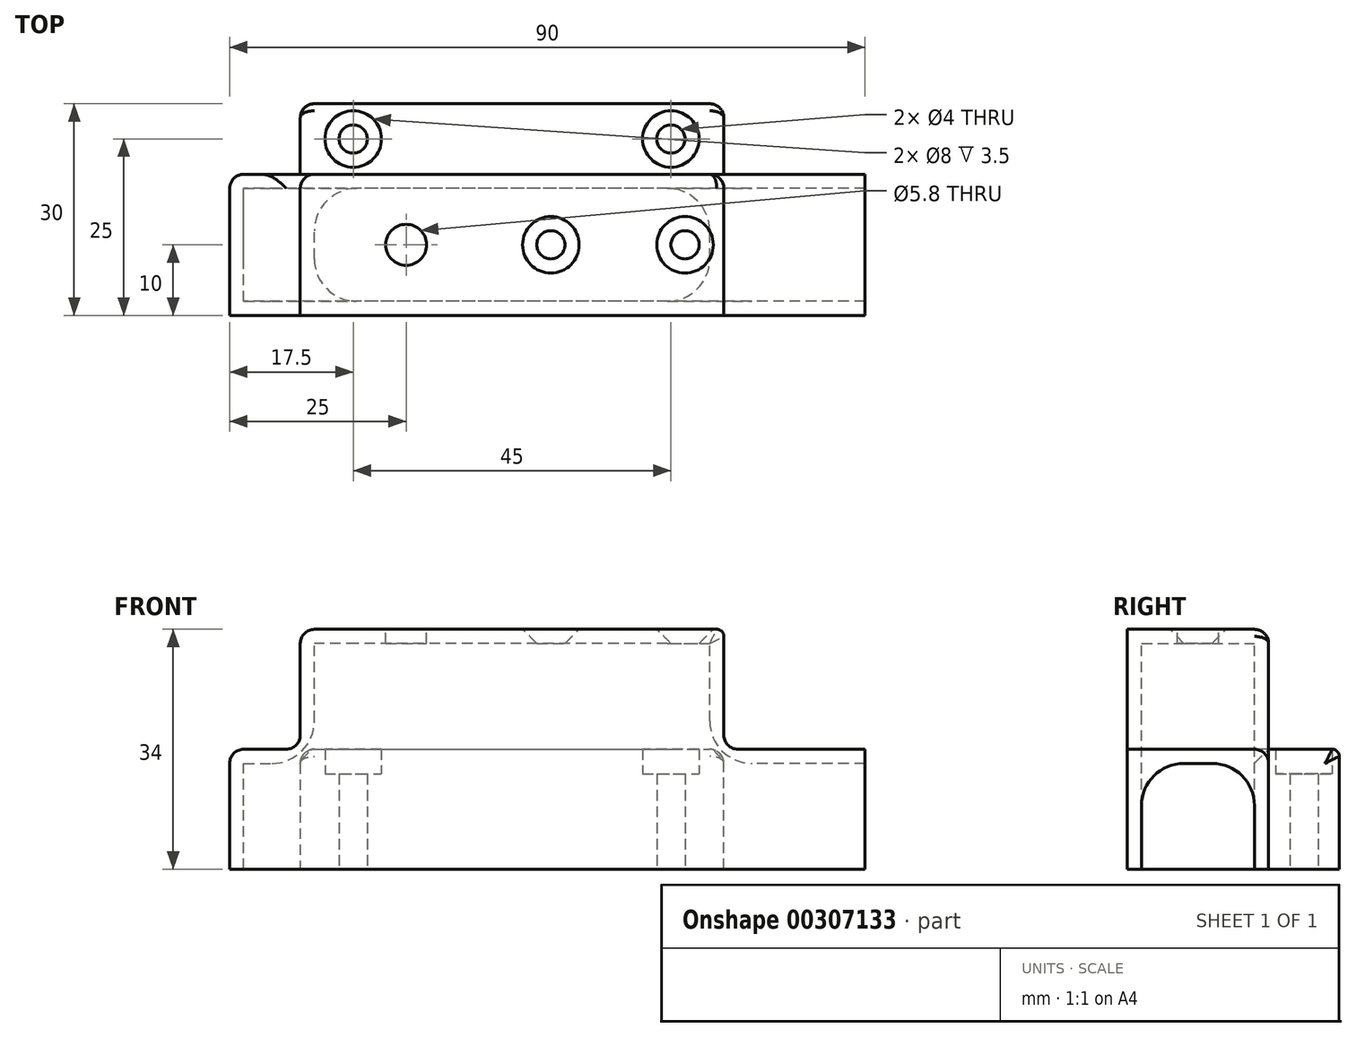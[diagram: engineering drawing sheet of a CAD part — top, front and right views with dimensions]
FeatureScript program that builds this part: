
annotation { "Feature Type Name" : "Feature", "Feature Type Description" : "" }
export const myFeature = defineFeature(function(context is Context, id is Id, definition is map)
    precondition{}
    {
        {
            var Q0;
            Q0=qCreatedBy(makeId("Front.planeOp"),FACE);
            var sketch = newSketch(context, id + "F0", { "sketchPlane" : qUnion([Q0])});
            skLineSegment(sketch, "E0", {"start": v(0, 0) * mm, "end": v(-40, 0) * mm});
            skLineSegment(sketch, "E1", {"start": v(-40, 0) * mm, "end": v(-40, 17) * mm});
            skLineSegment(sketch, "E2", {"start": v(-40, 17) * mm, "end": v(-30, 17) * mm});
            skLineSegment(sketch, "E3", {"start": v(-30, 17) * mm, "end": v(-30, 34) * mm});
            skLineSegment(sketch, "E4", {"start": v(-30, 34) * mm, "end": v(0, 34) * mm});
            skLineSegment(sketch, "E5.MirrorCS", {"start": v(30, 34) * mm, "end": v(0, 34) * mm});
            skLineSegment(sketch, "E6.MirrorCS", {"start": v(30, 17) * mm, "end": v(30, 34) * mm});
            skLineSegment(sketch, "E7.MirrorCS", {"start": v(50, 17) * mm, "end": v(30, 17) * mm});
            skLineSegment(sketch, "E8.MirrorCS", {"start": v(50, 0) * mm, "end": v(50, 17) * mm});
            skLineSegment(sketch, "E9.MirrorCS", {"start": v(0, 0) * mm, "end": v(50, 0) * mm});
            skLineSegment(sketch, "E10", {"start": v(-30, 17) * mm, "end": v(30, 17) * mm});
            skLineSegment(sketch, "E11", {"start": v(30, 0) * mm, "end": v(30, 17) * mm});
            skLineSegment(sketch, "E12", {"start": v(-30, 17) * mm, "end": v(-30, 0) * mm});
            skSolve(sketch);
        }
        {
            var Q0;
            Q0 = qSketchRegion(id + "F0", true);
            var Q1;
            Q1=makeQuery(id+"F0.imprint","IMPRINT",FACE,{"disambiguationData":[TD([[makeQuery(id+"F0.imprint","IMPRINT",EDGE,{"derivedFrom":sQuery(id+"F0.wireOp",EDGE,"E0")}),-1.0]])]});
            extrude(context, id + "F1", {"entities" : qUnion([Q0, Q1]), "depth" : 20 * mm});
        }
        {
            var Q0;
            Q0=makeQuery(id+"F1.opExtrude","SWEPT_FACE",FACE,{"disambiguationData":[OSD([sQuery(id+"F0.wireOp",EDGE,"E0"),sQuery(id+"F0.wireOp",EDGE,"E9.MirrorCS")])]});
            shell(context, id + "F2", {"entities" : qUnion([Q0]), "thickness" : 2 * mm});
        }
        {
            var Q0;
            Q0=makeQuery(id+"F1.opExtrude","SWEPT_FACE",FACE,{"disambiguationData":[OSD([sQuery(id+"F0.wireOp",EDGE,"E4"),sQuery(id+"F0.wireOp",EDGE,"E5.MirrorCS")])]});
            var sketch = newSketch(context, id + "F3", { "sketchPlane" : qUnion([Q0])});
            skLineSegment(sketch, "E13", {"start": v(0, 0) * mm, "end": v(0, -20) * mm});
            skLineSegment(sketch, "E14", {"start": v(0, -10) * mm, "end": v(-30, -10) * mm});
            skCircle(sketch, "E15", {"center": v(-15, -10) * mm, "radius": 2.9 * mm});
            skLineSegment(sketch, "E16.MirrorCS", {"start": v(0, -10) * mm, "end": v(30, -10) * mm});
            skLineSegment(sketch, "E17", {"start": v(15, -10) * mm, "end": v(11, -10) * mm});
            skLineSegment(sketch, "E18", {"start": v(11, -10) * mm, "end": v(11, -6.5) * mm});
            skLineSegment(sketch, "E19", {"start": v(11, -6.5) * mm, "end": v(15, -6.5) * mm});
            skLineSegment(sketch, "E20", {"start": v(15, -10) * mm, "end": v(15, -8.98) * mm});
            skLineSegment(sketch, "E21.MirrorCS", {"start": v(19, -10) * mm, "end": v(19, -6.5) * mm});
            skLineSegment(sketch, "E22.MirrorCS", {"start": v(19, -6.5) * mm, "end": v(15, -6.5) * mm});
            skLineSegment(sketch, "E23.MirrorCS", {"start": v(11, -10) * mm, "end": v(11, -13.5) * mm});
            skLineSegment(sketch, "E24.MirrorCS", {"start": v(11, -13.5) * mm, "end": v(15, -13.5) * mm});
            skLineSegment(sketch, "E25.MirrorCS", {"start": v(19, -13.5) * mm, "end": v(15, -13.5) * mm});
            skLineSegment(sketch, "E26.MirrorCS", {"start": v(19, -10) * mm, "end": v(19, -13.5) * mm});
            skLineSegment(sketch, "E27", {"start": v(19, -10) * mm, "end": v(30, -10) * mm});
            skLineSegment(sketch, "E28", {"start": v(24.5, -10) * mm, "end": v(24.5, -8.9) * mm});
            skLineSegment(sketch, "E29", {"start": v(11, -10) * mm, "end": v(0, -10) * mm});
            skLineSegment(sketch, "E30", {"start": v(5.5, -10) * mm, "end": v(5.5, -8.97) * mm});
            skSolve(sketch);
        }
        {
            var Q0;
            {var subQ0=sQuery(id+"F3.wireOp",EDGE,"E15");var subQ1=sQuery(id+"F3.wireOp",EDGE,"E14");var subQ2=makeQuery(id+"F3.imprint","INTERSECT",VERTEX,{"disambiguationData":[OD(0.0)],"derivedFrom":[subQ1,subQ0]});Q0=makeQuery(id+"F3.imprint","IMPRINT",FACE,{"disambiguationData":[TD([[makeQuery(id+"F3.imprint","IMPRINT",EDGE,{"disambiguationData":[TD([[subQ2,-1.0]])],"derivedFrom":subQ1}),1.0]])]});}
            var Q1;
            {var subQ0=sQuery(id+"F3.wireOp",EDGE,"E17");Q1=makeQuery(id+"F3.imprint","IMPRINT",FACE,{"disambiguationData":[TD([[makeQuery(id+"F3.imprint","IMPRINT",EDGE,{"derivedFrom":subQ0}),-1.0]])]});}
            var Q2;
            {var subQ0=sQuery(id+"F3.wireOp",EDGE,"E17");Q2=makeQuery(id+"F3.imprint","IMPRINT",FACE,{"disambiguationData":[TD([[makeQuery(id+"F3.imprint","IMPRINT",EDGE,{"derivedFrom":subQ0}),1.0]])]});}
            var Q3;
            {var subQ0=sQuery(id+"F3.wireOp",EDGE,"E15");var subQ1=sQuery(id+"F3.wireOp",EDGE,"E14");var subQ2=makeQuery(id+"F3.imprint","INTERSECT",VERTEX,{"disambiguationData":[OD(0.0)],"derivedFrom":[subQ1,subQ0]});Q3=makeQuery(id+"F3.imprint","IMPRINT",FACE,{"disambiguationData":[TD([[makeQuery(id+"F3.imprint","IMPRINT",EDGE,{"disambiguationData":[TD([[subQ2,-1.0]])],"derivedFrom":subQ1}),-1.0]])]});}
            extrude(context, id + "F4", {"entities" : qUnion([Q0, Q1, Q2, Q3]), "operationType" : NewBodyOperationType.REMOVE, "oppositeDirection" : true, "depth" : 3 * mm});
        }
        {
            var Q0;
            Q0=makeQuery(id+"F2.opShell","OFFSET_FACE",FACE,{"disambiguationData":[OSD([sQuery(id+"F0.wireOp",EDGE,"E8.MirrorCS")])]});
            extrude(context, id + "F5", {"entities" : qUnion([Q0]), "operationType" : NewBodyOperationType.REMOVE, "oppositeDirection" : true, "depth" : 25 * mm});
        }
        {
            var Q0;
            Q0=makeQuery(id+"F2.opShell","OFFSET_EDGE",EDGE,{"disambiguationData":[OSD([sQuery(id+"F0.wireOp",EDGE,"E6.MirrorCS"),sQuery(id+"F0.wireOp",EDGE,"E7.MirrorCS")])]});
            var Q1;
            Q1=makeQuery(id+"F2.opShell","OFFSET_EDGE",EDGE,{"disambiguationData":[OSD([sQuery(id+"F0.wireOp",EDGE,"E2"),sQuery(id+"F0.wireOp",EDGE,"E3")])]});
            fillet(context, id + "F6", {"entities" : qUnion([Q0, Q1]), "radius" : 6 * mm, "tangentPropagation" : true, "allowEdgeOverflow" : false});
        }
        {
            var Q0;
            Q0=makeQuery(id+"F1.opExtrude","SWEPT_EDGE",EDGE,{"disambiguationData":[OSD([sQuery(id+"F0.wireOp",EDGE,"E3"),sQuery(id+"F0.wireOp",EDGE,"E4")])]});
            var Q1;
            Q1=makeQuery(id+"F1.opExtrude","SWEPT_EDGE",EDGE,{"disambiguationData":[OSD([sQuery(id+"F0.wireOp",EDGE,"E1"),sQuery(id+"F0.wireOp",EDGE,"E2")])]});
            var Q2;
            Q2=makeQuery(id+"F1.opExtrude","SWEPT_EDGE",EDGE,{"disambiguationData":[OSD([sQuery(id+"F0.wireOp",EDGE,"E2"),sQuery(id+"F0.wireOp",EDGE,"E3")])]});
            var Q3;
            Q3=makeQuery(id+"F1.opExtrude","CAP_EDGE",EDGE,{"disambiguationData":[OSD([sQuery(id+"F0.wireOp",EDGE,"E4"),sQuery(id+"F0.wireOp",EDGE,"E5.MirrorCS")])],"isStart":true});
            var Q4;
            Q4=makeQuery(id+"F1.opExtrude","CAP_EDGE",EDGE,{"disambiguationData":[OSD([sQuery(id+"F0.wireOp",EDGE,"E6.MirrorCS")])],"isStart":true});
            var Q5;
            Q5=makeQuery(id+"F1.opExtrude","CAP_EDGE",EDGE,{"disambiguationData":[OSD([sQuery(id+"F0.wireOp",EDGE,"E7.MirrorCS")])],"isStart":true});
            var Q6;
            Q6=makeQuery(id+"F1.opExtrude","SWEPT_EDGE",EDGE,{"disambiguationData":[OSD([sQuery(id+"F0.wireOp",EDGE,"E6.MirrorCS"),sQuery(id+"F0.wireOp",EDGE,"E7.MirrorCS")])]});
            var Q7;
            Q7=makeQuery(id+"F1.opExtrude","CAP_EDGE",EDGE,{"disambiguationData":[OSD([sQuery(id+"F0.wireOp",EDGE,"E3")])],"isStart":true});
            var Q8;
            Q8=makeQuery(id+"F1.opExtrude","CAP_EDGE",EDGE,{"disambiguationData":[OSD([sQuery(id+"F0.wireOp",EDGE,"E1")])],"isStart":true});
            fillet(context, id + "F7", {"entities" : qUnion([Q0, Q1, Q2, Q3, Q4, Q5, Q6, Q7, Q8]), "radius" : 2 * mm, "tangentPropagation" : true, "allowEdgeOverflow" : false});
        }
        {
            var Q0;
            Q0=sQuery(id+"F3.wireOp",VERTEX,"E30.start");
            var Q1;
            Q1=sQuery(id+"F3.wireOp",VERTEX,"E28.start");
            var Q2;
            Q2=makeQuery(id+"F1.opExtrude","SWEPT_BODY",BODY,{"disambiguationData":[OSD([sQuery(id+"F0.wireOp",EDGE,"E0"),sQuery(id+"F0.wireOp",EDGE,"E1"),sQuery(id+"F0.wireOp",EDGE,"E2"),sQuery(id+"F0.wireOp",EDGE,"E3"),sQuery(id+"F0.wireOp",EDGE,"E4"),sQuery(id+"F0.wireOp",EDGE,"E5.MirrorCS"),sQuery(id+"F0.wireOp",EDGE,"E6.MirrorCS"),sQuery(id+"F0.wireOp",EDGE,"E7.MirrorCS"),sQuery(id+"F0.wireOp",EDGE,"E8.MirrorCS"),sQuery(id+"F0.wireOp",EDGE,"E9.MirrorCS")])]});
            hole(context, id + "F8", {"style" : HoleStyle.C_SINK, "endStyle" : HoleEndStyle.THROUGH, "holeDiameter" : 2.6 * mm, "cSinkDiameter" : 8 * mm, "cSinkAngle" : 90 * degree, "tappedDepth" : 12 * mm, "tapClearance" : 3, "locations" : qUnion([Q0, Q1]), "scope" : qUnion([Q2]), "startStyle" : HoleStartStyle.PART});
        }
        {
            var Q0;
            Q0=makeQuery(id+"F1.opExtrude","SWEPT_EDGE",EDGE,{"disambiguationData":[OSD([sQuery(id+"F0.wireOp",EDGE,"E5.MirrorCS"),sQuery(id+"F0.wireOp",EDGE,"E6.MirrorCS")])]});
            fillet(context, id + "F9", {"entities" : qUnion([Q0]), "radius" : 1 * mm, "tangentPropagation" : true, "allowEdgeOverflow" : false});
        }
        {
            var Q0;
            Q0=makeQuery(id+"F0.imprint","IMPRINT",FACE,{"disambiguationData":[TD([[makeQuery(id+"F0.imprint","IMPRINT",EDGE,{"derivedFrom":sQuery(id+"F0.wireOp",EDGE,"E10")}),-1.0]])]});
            extrude(context, id + "F10", {"entities" : qUnion([Q0]), "operationType" : NewBodyOperationType.ADD, "oppositeDirection" : true, "depth" : 10 * mm});
        }
        {
            var Q0;
            Q0=makeQuery(id+"F10.opExtrude","SWEPT_FACE",FACE,{"disambiguationData":[OSD([sQuery(id+"F0.wireOp",EDGE,"E10")])]});
            var sketch = newSketch(context, id + "F11", { "sketchPlane" : qUnion([Q0])});
            skLineSegment(sketch, "E31", {"start": v(-30, 5) * mm, "end": v(30, 5) * mm});
            skLineSegment(sketch, "E32", {"start": v(30, 5) * mm, "end": v(0, 5) * mm});
            skLineSegment(sketch, "E33", {"start": v(0, 5) * mm, "end": v(-30, 5) * mm});
            skLineSegment(sketch, "E34", {"start": v(-15, 5) * mm, "end": v(-30, 5) * mm});
            skLineSegment(sketch, "E35", {"start": v(-22.5, 5) * mm, "end": v(-22.5, 8) * mm});
            skLineSegment(sketch, "E36", {"start": v(30, 5) * mm, "end": v(22.5, 5) * mm});
            skSolve(sketch);
        }
        {
            var Q0;
            Q0=sQuery(id+"F11.wireOp",VERTEX,"E35.start");
            var Q1;
            Q1=sQuery(id+"F11.wireOp",VERTEX,"E36.end");
            var Q2;
            Q2=makeQuery(id+"F1.opExtrude","SWEPT_BODY",BODY,{"disambiguationData":[OSD([sQuery(id+"F0.wireOp",EDGE,"E0"),sQuery(id+"F0.wireOp",EDGE,"E1"),sQuery(id+"F0.wireOp",EDGE,"E2"),sQuery(id+"F0.wireOp",EDGE,"E3"),sQuery(id+"F0.wireOp",EDGE,"E4"),sQuery(id+"F0.wireOp",EDGE,"E5.MirrorCS"),sQuery(id+"F0.wireOp",EDGE,"E6.MirrorCS"),sQuery(id+"F0.wireOp",EDGE,"E7.MirrorCS"),sQuery(id+"F0.wireOp",EDGE,"E8.MirrorCS"),sQuery(id+"F0.wireOp",EDGE,"E9.MirrorCS")])]});
            hole(context, id + "F12", {"style" : HoleStyle.C_BORE, "endStyle" : HoleEndStyle.THROUGH, "holeDiameter" : 4 * mm, "cBoreDiameter" : 8 * mm, "cBoreDepth" : 3.5 * mm, "tappedDepth" : 12 * mm, "tapClearance" : 3, "locations" : qUnion([Q0, Q1]), "scope" : qUnion([Q2]), "startStyle" : HoleStartStyle.PART});
        }
        {
            var Q0;
            Q0=makeQuery(id+"F10.opExtrude","SWEPT_EDGE",EDGE,{"disambiguationData":[OSD([sQuery(id+"F0.wireOp",EDGE,"E6.MirrorCS"),sQuery(id+"F0.wireOp",EDGE,"E7.MirrorCS"),sQuery(id+"F0.wireOp",EDGE,"E10"),sQuery(id+"F0.wireOp",EDGE,"E11")])]});
            var Q1;
            Q1=makeQuery(id+"F10.opExtrude","CAP_EDGE",EDGE,{"disambiguationData":[OSD([sQuery(id+"F0.wireOp",EDGE,"E11")])],"isStart":false});
            var Q2;
            Q2=makeQuery(id+"F10.opExtrude","SWEPT_EDGE",EDGE,{"disambiguationData":[OSD([sQuery(id+"F0.wireOp",EDGE,"E2"),sQuery(id+"F0.wireOp",EDGE,"E3"),sQuery(id+"F0.wireOp",EDGE,"E10"),sQuery(id+"F0.wireOp",EDGE,"E12")])]});
            var Q3;
            Q3=makeQuery(id+"F10.opExtrude","CAP_EDGE",EDGE,{"disambiguationData":[OSD([sQuery(id+"F0.wireOp",EDGE,"E12")])],"isStart":false});
            fillet(context, id + "F13", {"entities" : qUnion([Q0, Q1, Q2, Q3]), "radius" : 2 * mm, "tangentPropagation" : true, "allowEdgeOverflow" : false});
        }
        {
            var Q0;
            Q0=makeQuery(id+"F10.opExtrude","CAP_EDGE",EDGE,{"disambiguationData":[OSD([sQuery(id+"F0.wireOp",EDGE,"E10")])],"isStart":false});
            fillet(context, id + "F14", {"entities" : qUnion([Q0]), "radius" : 1 * mm, "tangentPropagation" : true, "allowEdgeOverflow" : false});
        }
    });
